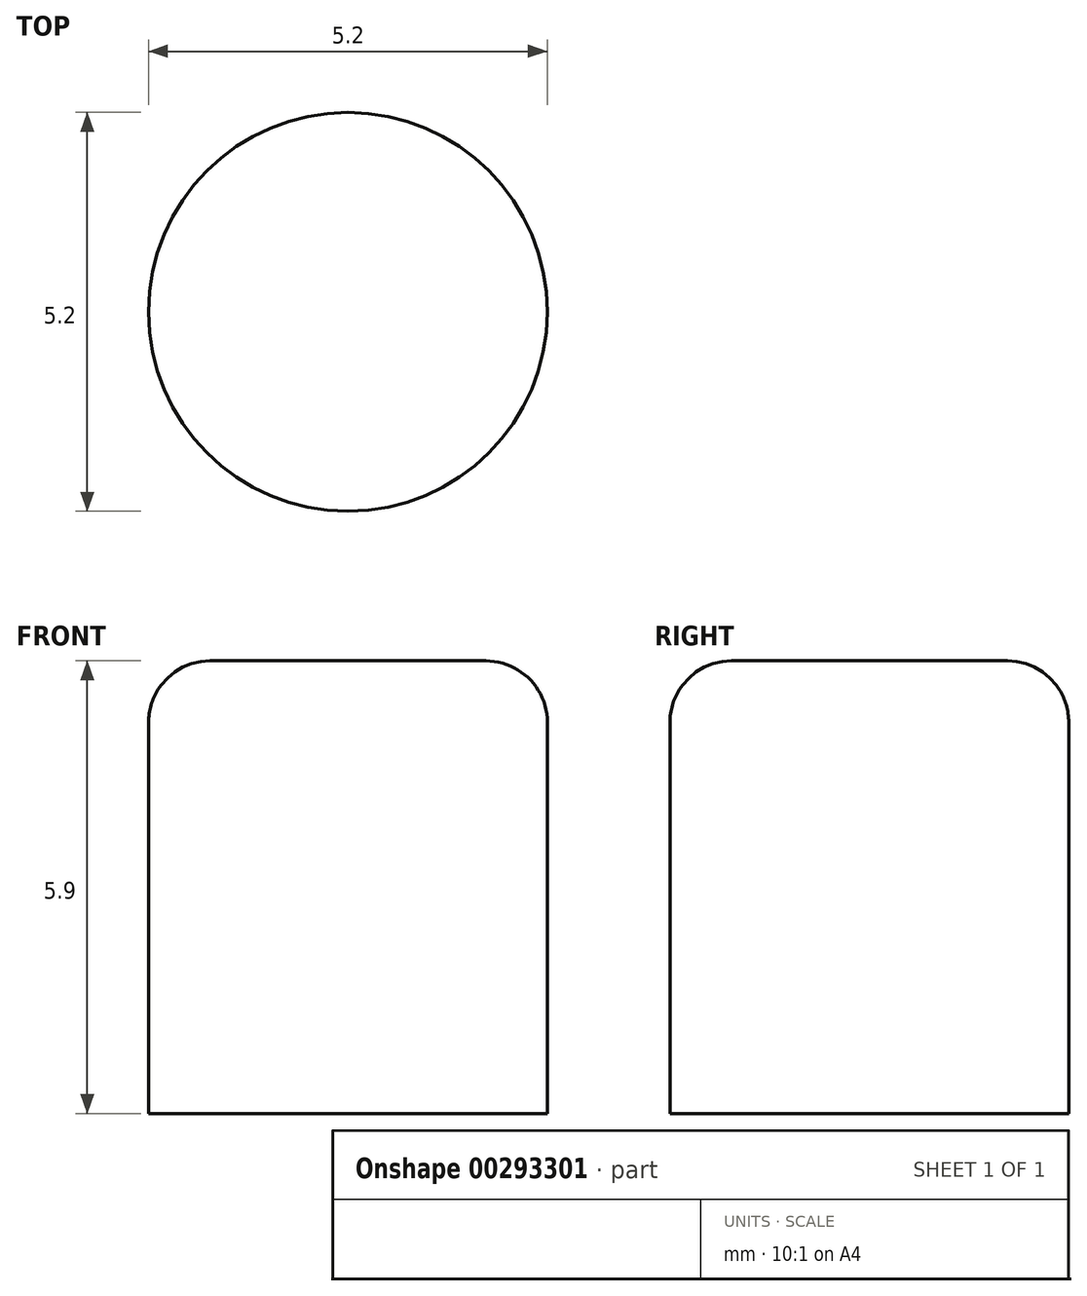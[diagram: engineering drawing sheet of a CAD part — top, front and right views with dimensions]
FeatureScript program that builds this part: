
annotation { "Feature Type Name" : "Feature", "Feature Type Description" : "" }
export const myFeature = defineFeature(function(context is Context, id is Id, definition is map)
    precondition{}
    {
        {
            var Q0;
            Q0=qCreatedBy(makeId("Top.planeOp"),FACE);
            var sketch = newSketch(context, id + "F0", { "sketchPlane" : qUnion([Q0])});
            skCircle(sketch, "E0", {"center": v(0, 0) * mm, "radius": 2.6 * mm});
            skSolve(sketch);
        }
        {
            var Q0;
            Q0=qSketchRegion(id+"F0",true);
            extrude(context, id + "F1", {"entities" : qUnion([Q0]), "flatOperationType" : FlatOperationType.REMOVE, "offsetDistance" : 25 * mm, "depth" : 5.9 * mm, "domain" : OperationDomain.MODEL});
        }
        {
            var Q0;
            Q0=makeQuery(id+"F1.opExtrude","CAP_FACE",FACE,{"disambiguationData":[OSD([sQuery(id+"F0.wireOp",EDGE,"E0")])],"isStart":false});
            fillet(context, id + "F2", {"entities" : qUnion([Q0]), "radius" : .8 * mm, "tangentPropagation" : true, "allowEdgeOverflow" : false});
        }
    });
